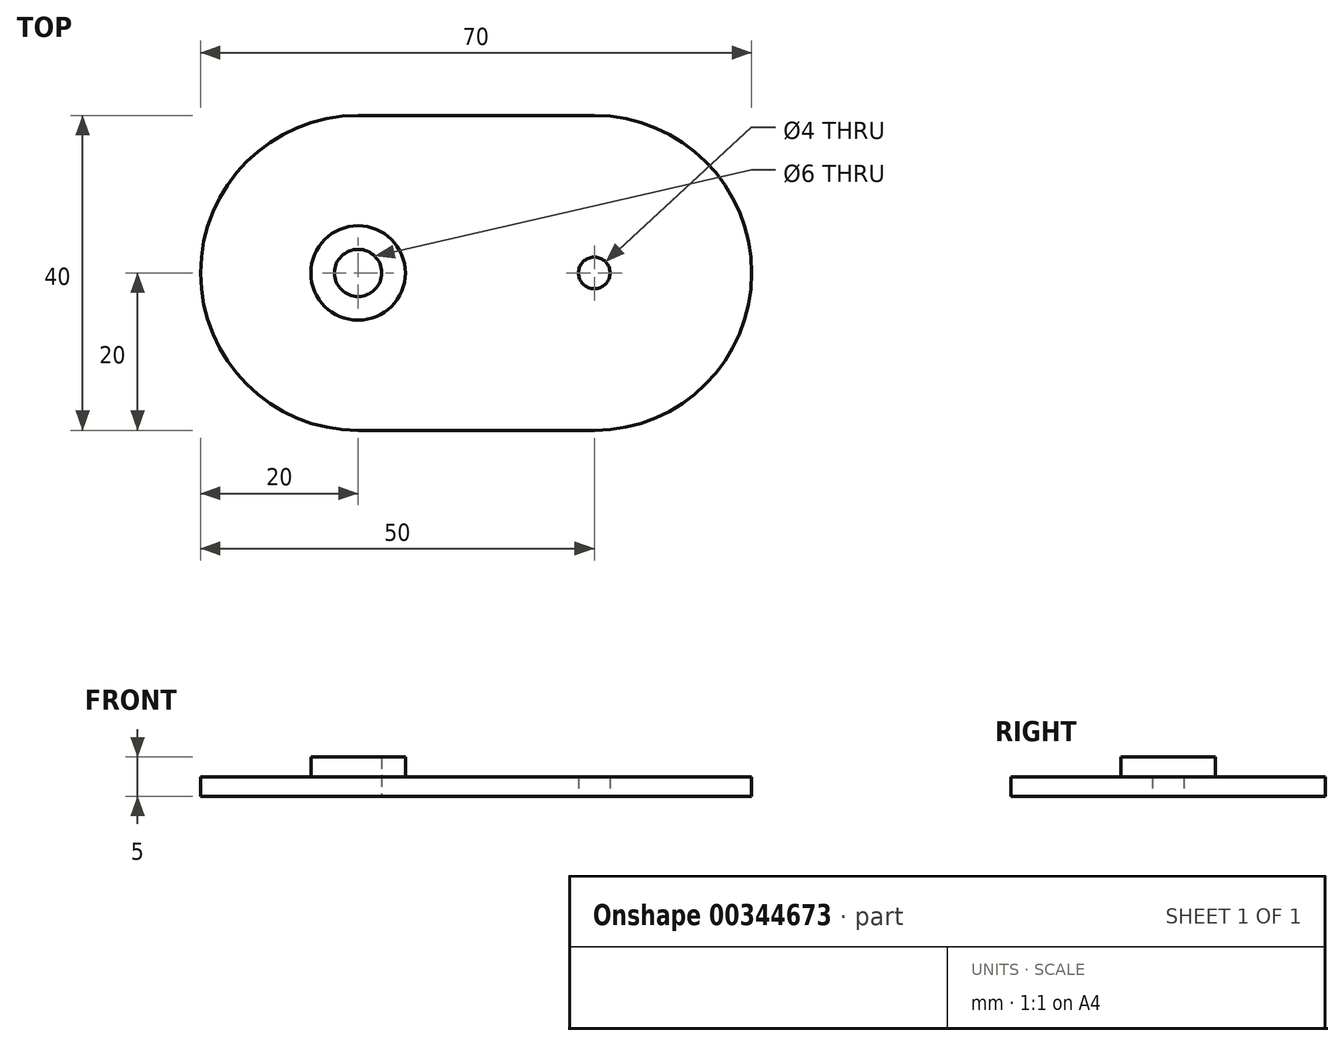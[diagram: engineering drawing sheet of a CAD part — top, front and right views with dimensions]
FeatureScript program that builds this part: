
annotation { "Feature Type Name" : "Feature", "Feature Type Description" : "" }
export const myFeature = defineFeature(function(context is Context, id is Id, definition is map)
    precondition{}
    {
        {
            var Q0;
            Q0=qCreatedBy(makeId("Top.planeOp"),FACE);
            var sketch = newSketch(context, id + "F0", { "sketchPlane" : qUnion([Q0])});
            skLineSegment(sketch, "E0", {"start": v(-15, 20) * mm, "end": v(15, 20) * mm});
            skLineSegment(sketch, "E1", {"start": v(-15, -20) * mm, "end": v(15, -20) * mm});
            skArc(sketch, "E2", {"start": v(15, 20) * mm, "mid": v(35, 0) * mm, "end": v(15, -20) * mm});
            skArc(sketch, "E3", {"start": v(-15, 20) * mm, "mid": v(-35, 0) * mm, "end": v(-15, -20) * mm});
            skCircle(sketch, "E4", {"center": v(-15, 0) * mm, "radius": 3 * mm});
            skCircle(sketch, "E5", {"center": v(15, 0) * mm, "radius": 2 * mm});
            skPoint(sketch, "E6", {"position": v(0, 20) * mm});
            skPoint(sketch, "E7", {"position": v(35, 0) * mm});
            skCircle(sketch, "E8", {"center": v(-15, 0) * mm, "radius": 6 * mm});
            skSolve(sketch);
        }
        {
            var Q0;
            Q0=makeQuery(id+"F0.imprint","IMPRINT",FACE,{"disambiguationData":[TD([[makeQuery(id+"F0.imprint","IMPRINT",EDGE,{"derivedFrom":sQuery(id+"F0.wireOp",EDGE,"E0")}),-1.0]])]});
            extrude(context, id + "F1", {"entities" : qUnion([Q0]), "depth" : 2.5 * mm});
        }
        {
            var Q0;
            Q0=makeQuery(id+"F0.imprint","IMPRINT",FACE,{"disambiguationData":[TD([[makeQuery(id+"F0.imprint","IMPRINT",EDGE,{"derivedFrom":sQuery(id+"F0.wireOp",EDGE,"E4")}),-1.0]])]});
            extrude(context, id + "F2", {"entities" : qUnion([Q0]), "operationType" : NewBodyOperationType.ADD, "depth" : 5 * mm});
        }
    });
